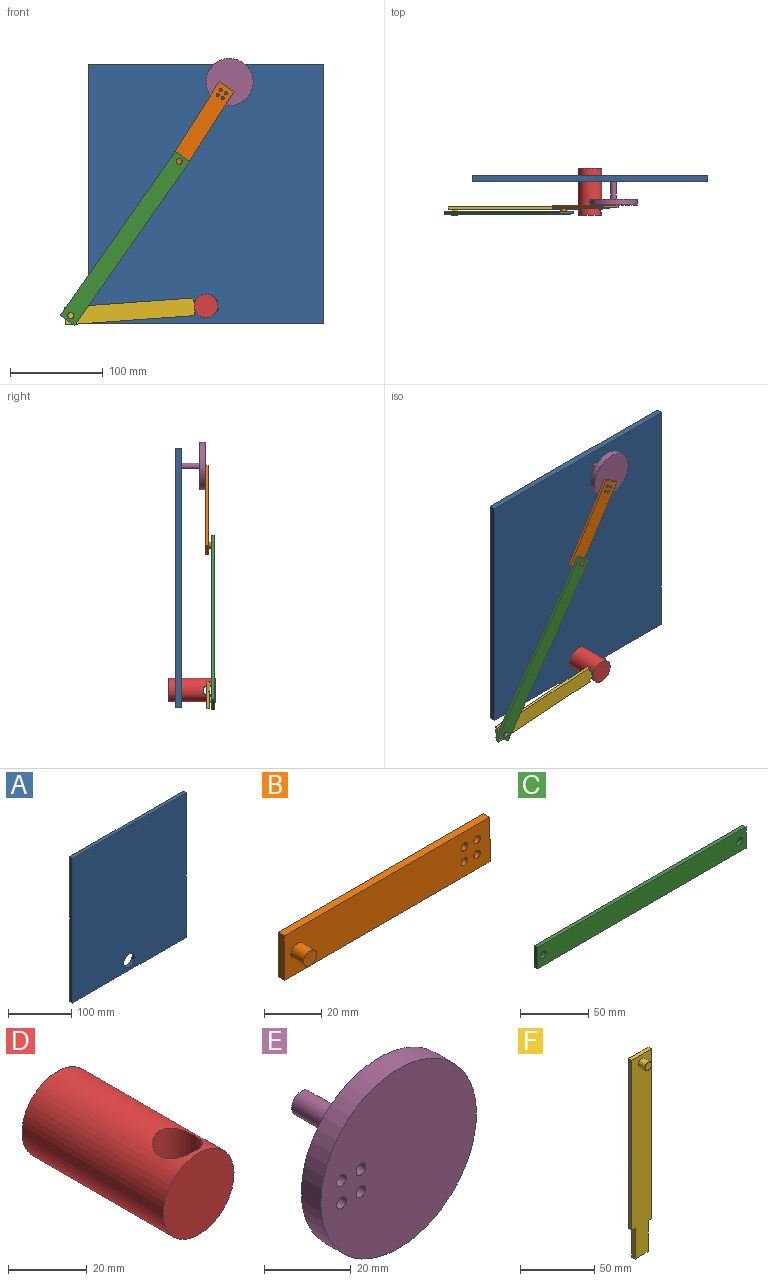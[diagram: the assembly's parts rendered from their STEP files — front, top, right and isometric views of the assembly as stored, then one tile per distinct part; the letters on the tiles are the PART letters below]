
ASSEMBLY  parts=6 mates=9
PART A: 8 faces, bbox 254x6.4x279.4 mm
  f0: plane 254x6.35mm, normal (0,0,1), area 1612.9mm2, adj f1,f5,f6,f7
  f1: plane 279.4x6.35mm, normal (-1,0,0), area 1774.2mm2, adj f0,f2,f6,f7
  f2: plane 254x6.35mm, normal (0,0,-1), area 1612.9mm2, adj f1,f5,f6,f7
  f3: cylinder r=12.7mm len=25.4mm, axis (0,-1,0), area 506.7mm2, adj f6,f7
  f4: cylinder r=3.17mm len=6.35mm, axis (0,-1,0), area 126.7mm2, adj f6,f7
  f5: plane 279.4x6.35mm, normal (1,0,0), area 1774.2mm2, adj f0,f2,f6,f7
  f6: plane 279.4x254mm, normal (0,1,0), area 70429.2mm2, adj f0,f1,f2,f3,f4,f5
  f7: plane 279.4x254mm, normal (0,-1,0), area 70429.2mm2, adj f0,f1,f2,f3,f4,f5
PART B: 12 faces, bbox 101.6x9.5x19.1 mm
  f0: plane 101.6x3.18mm, normal (0,0,-1), area 322.6mm2, adj f1,f7,f8,f9
  f1: plane 19.05x3.18mm, normal (1,0,0), area 60.5mm2, adj f0,f2,f8,f9
  f2: plane 101.6x3.18mm, normal (0,0,1), area 322.6mm2, adj f1,f7,f8,f9
  f3: cylinder r=1.59mm len=3.18mm, axis (0,1,0), area 31.7mm2, adj f8,f9
  f4: cylinder r=1.59mm len=3.18mm, axis (0,1,0), area 31.7mm2, adj f8,f9
  f5: cylinder r=1.59mm len=3.18mm, axis (0,1,0), area 31.7mm2, adj f8,f9
  f6: cylinder r=1.59mm len=3.18mm, axis (0,1,0), area 31.7mm2, adj f8,f9
  f7: plane 19.05x3.18mm, normal (-1,0,0), area 60.5mm2, adj f0,f2,f8,f9
  f8: plane 101.6x19.05mm, normal (0,-1,0), area 1872.1mm2, adj f0,f1,f2,f3,f4,f5,f6,f7
  f9: plane 101.6x19.05mm, normal (0,1,0), area 1903.8mm2, adj f0,f1,f2,f3,f4,f5,f6,f7
  f10: cylinder r=3.17mm len=6.35mm, axis (0,1,0), area 126.7mm2, adj f8,f11
  f11: plane 6.35x6.35mm, normal (0,-1,0), area 31.7mm2, adj f10
PART C: 8 faces, bbox 215.9x3.2x19.1 mm
  f0: plane 215.9x3.18mm, normal (0,0,-1), area 685.5mm2, adj f1,f3,f4,f5
  f1: plane 19.05x3.18mm, normal (1,0,0), area 60.5mm2, adj f0,f2,f4,f5
  f2: plane 215.9x3.18mm, normal (0,0,1), area 685.5mm2, adj f1,f3,f4,f5
  f3: plane 19.05x3.18mm, normal (-1,0,0), area 60.5mm2, adj f0,f2,f4,f5
  f4: plane 215.9x19.05mm, normal (0,-1,0), area 4049.6mm2, adj f0,f1,f2,f3,f6,f7
  f5: plane 215.9x19.05mm, normal (0,1,0), area 4049.6mm2, adj f0,f1,f2,f3,f6,f7
  f6: cylinder r=3.17mm len=6.35mm, axis (0,-1,0), area 63.3mm2, adj f4,f5
  f7: cylinder r=3.17mm len=6.35mm, axis (0,-1,0), area 63.3mm2, adj f4,f5
PART D: 5 faces, bbox 25.4x50.8x25.4 mm
  f0: cylinder r=12.7mm len=50.8mm, axis (0,1,0), area 3817.1mm2, adj f1,f2,f3,f4
  f1: plane 25.4x25.4mm, normal (0,-1,0), area 506.7mm2, adj f0
  f2: plane 25.4x25.4mm, normal (0,1,0), area 506.7mm2, adj f0
  f3: cone r=6.35mm half-angle=3deg, axis (0,0,1), area 456.5mm2, adj f0,f4
  f4: cylinder r=6.35mm len=12.7mm, axis (0,0,1), area 473.4mm2, adj f0,f3
PART E: 9 faces, bbox 50.8x31.8x50.8 mm
  f0: cylinder r=1.59mm len=6.35mm, axis (0,1,0), area 63.3mm2, adj f5,f6
  f1: cylinder r=1.59mm len=6.35mm, axis (0,1,0), area 63.3mm2, adj f5,f6
  f2: cylinder r=1.59mm len=6.35mm, axis (0,1,0), area 63.3mm2, adj f5,f6
  f3: cylinder r=1.59mm len=6.35mm, axis (0,1,0), area 63.3mm2, adj f5,f6
  f4: cylinder r=25.4mm len=50.8mm, axis (0,1,0), area 1013.4mm2, adj f5,f6
  f5: plane 50.8x50.8mm, normal (0,-1,0), area 1995.2mm2, adj f0,f1,f2,f3,f4
  f6: plane 50.8x50.8mm, normal (0,1,0), area 1963.5mm2, adj f0,f1,f2,f3,f4,f7
  f7: cylinder r=3.17mm len=25.4mm, axis (0,-1,0), area 506.7mm2, adj f6,f8
  f8: plane 6.35x6.35mm, normal (0,1,0), area 31.7mm2, adj f7
PART F: 12 faces, bbox 19.1x9.5x165.1 mm
  f0: plane 12.7x3.18mm, normal (0,0,-1), area 39.9mm2, adj f1,f7,f10,f11
  f1: plane 165.1x19.05mm, normal (0,-1,0), area 2942mm2, adj f0,f2,f3,f4,f5,f6,f8,f10
  f2: plane 139.7x3.18mm, normal (-1,0,0), area 443.5mm2, adj f1,f3,f6,f7
  f3: plane 3.38x3.18mm, normal (0,0,-1), area 10.3mm2, adj f1,f2,f7,f11
  f4: plane 3.38x3.18mm, normal (0,0,-1), area 10.3mm2, adj f1,f5,f7,f10
  f5: plane 139.7x3.18mm, normal (1,0,0), area 443.5mm2, adj f1,f4,f6,f7
  f6: plane 19.05x3.18mm, normal (0,0,1), area 60.5mm2, adj f1,f2,f5,f7
  f7: plane 165.1x19.05mm, normal (0,1,0), area 2973.6mm2, adj f0,f2,f3,f4,f5,f6,f10,f11
  f8: cylinder r=3.17mm len=6.35mm, axis (0,1,0), area 126.7mm2, adj f1,f9
  f9: plane 6.35x6.35mm, normal (0,-1,0), area 31.7mm2, adj f8
  f10: cylinder r=6.35mm len=25.4mm, axis (0,0,-1), area 81.5mm2, adj f0,f1,f4,f7
  f11: cylinder r=6.35mm len=25.4mm, axis (0,0,-1), area 81.5mm2, adj f0,f1,f3,f7
PLACE A t=(-38.83,-71.54,215.39)mm fixed
PLACE B rot(axis=(0,-1,0),57.5deg) t=(-303.19,-96.94,320.75)mm
PLACE C rot(axis=(0,-1,0),55deg) t=(-350.89,-103.29,245.22)mm
PLACE D rot(axis=(0,1,0),85.9deg) t=(-333.44,-56.94,89.58)mm
PLACE E rot(axis=(0,-1,0),57.5deg) t=(-308.04,-90.59,330.88)mm
PLACE F rot(axis=(0,-1,0),94.1deg) t=(-329.91,-98.53,80.28)mm
MATE planar E.f7 <-> A.f6  axis (0,1,0) through (-308.04,-65.19,330.88)mm
MATE cylindrical E.f0 <-> B.f3  axis (0,1,0) through (-320.72,-96.94,316.85)mm
MATE cylindrical A.f3 <-> D.f0  axis (0,1,0) through (-333.44,-65.19,89.58)mm
MATE planar E.f3 <-> B.f9  axis (0,-1,0) through (-315.36,-96.94,313.44)mm
MATE cylindrical E.f7 <-> A.f4  axis (0,1,0) through (-308.04,-65.19,330.88)mm
MATE revolute D.f3 <-> F.f10  axis (1,0,0.07) through (-320.68,-100.12,90.49)mm
MATE revolute F.f8 <-> C.f7  axis (0,1,0) through (-479.02,-104.88,79.13)mm
MATE cylindrical B.f4 <-> E.f1  axis (0,1,0) through (-317.32,-96.94,322.21)mm
MATE revolute B.f10 <-> C.f6  axis (0,-1,0) through (-362.34,-106.47,245.49)mm
